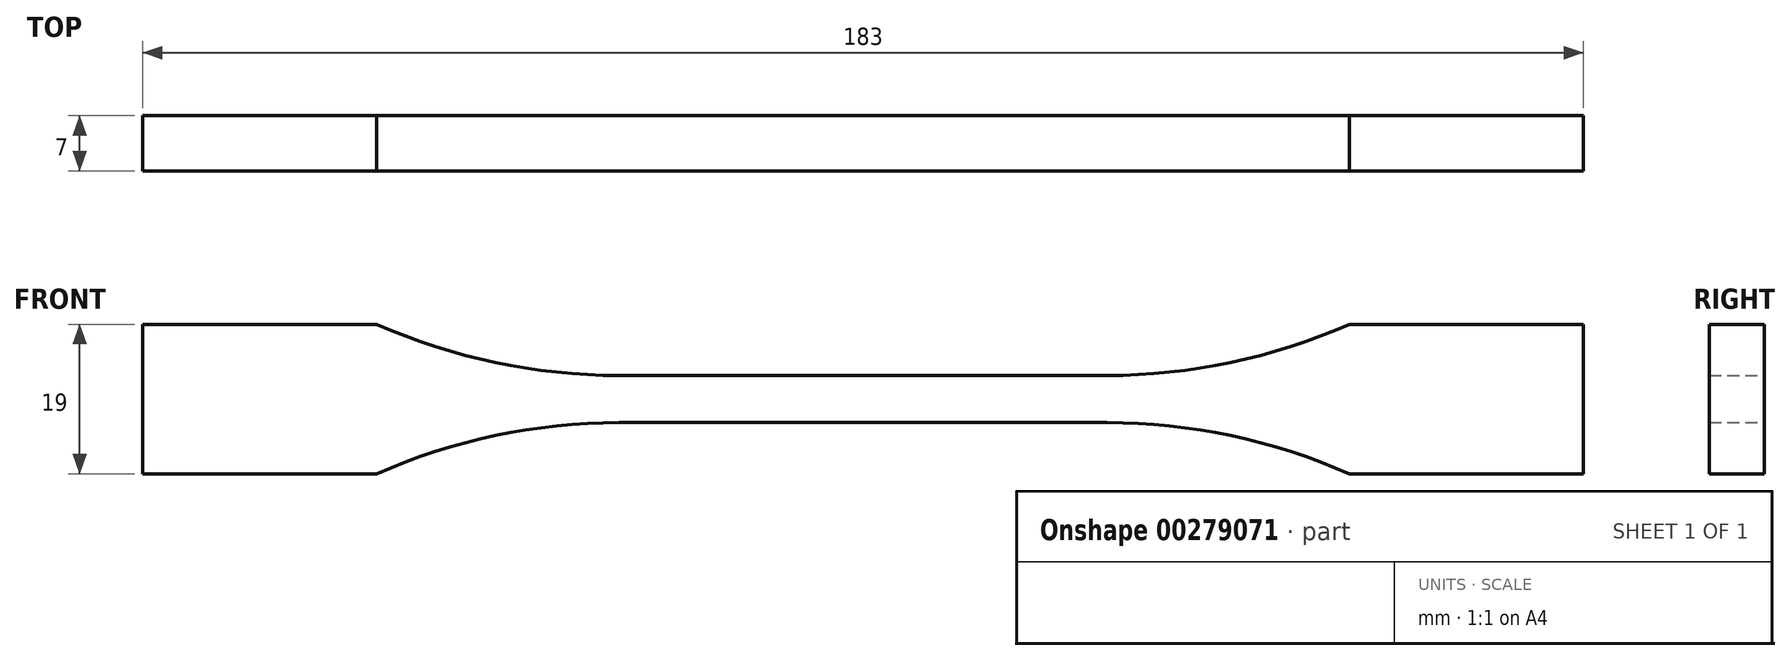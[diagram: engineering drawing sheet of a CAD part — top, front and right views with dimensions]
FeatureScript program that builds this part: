
annotation { "Feature Type Name" : "Feature", "Feature Type Description" : "" }
export const myFeature = defineFeature(function(context is Context, id is Id, definition is map)
    precondition{}
    {
        {
            var Q0;
            Q0=qCreatedBy(makeId("Front.planeOp"),FACE);
            var sketch = newSketch(context, id + "F0", { "sketchPlane" : qUnion([Q0])});
            skLineSegment(sketch, "E0", {"start": v(0, 3) * mm, "end": v(31, 3) * mm});
            skArc(sketch, "E1", {"start": v(31, 3) * mm, "mid": v(46.73, 4.64) * mm, "end": v(61.76, 9.5) * mm});
            skLineSegment(sketch, "E2", {"start": v(61.76, 9.5) * mm, "end": v(91.5, 9.5) * mm});
            skLineSegment(sketch, "E3.MirrorCS", {"start": v(61.76, -9.5) * mm, "end": v(91.5, -9.5) * mm});
            skLineSegment(sketch, "E4.MirrorCS", {"start": v(0, -3) * mm, "end": v(31, -3) * mm});
            skArc(sketch, "E5.MirrorCS", {"start": v(31, -3) * mm, "mid": v(46.73, -4.64) * mm, "end": v(61.76, -9.5) * mm});
            skArc(sketch, "E6.MirrorCS", {"start": v(-31, -3) * mm, "mid": v(-46.73, -4.64) * mm, "end": v(-61.76, -9.5) * mm});
            skLineSegment(sketch, "E7.MirrorCS", {"start": v(0, 3) * mm, "end": v(-31, 3) * mm});
            skArc(sketch, "E8.MirrorCS", {"start": v(-31, 3) * mm, "mid": v(-46.73, 4.64) * mm, "end": v(-61.76, 9.5) * mm});
            skLineSegment(sketch, "E9.MirrorCS", {"start": v(-61.76, -9.5) * mm, "end": v(-91.5, -9.5) * mm});
            skLineSegment(sketch, "E10.MirrorCS", {"start": v(0, -3) * mm, "end": v(-31, -3) * mm});
            skLineSegment(sketch, "E11.MirrorCS", {"start": v(-61.76, 9.5) * mm, "end": v(-91.5, 9.5) * mm});
            skLineSegment(sketch, "E12", {"start": v(-91.5, 9.5) * mm, "end": v(-91.5, -9.5) * mm});
            skLineSegment(sketch, "E13", {"start": v(91.5, 9.5) * mm, "end": v(91.5, -9.5) * mm});
            skSolve(sketch);
        }
        {
            var Q0;
            Q0 = qSketchRegion(id + "F0", true);
            extrude(context, id + "F1", {"entities" : qUnion([Q0]), "endBound" : BoundingType.SYMMETRIC, "depth" : 7 * mm});
        }
    });
